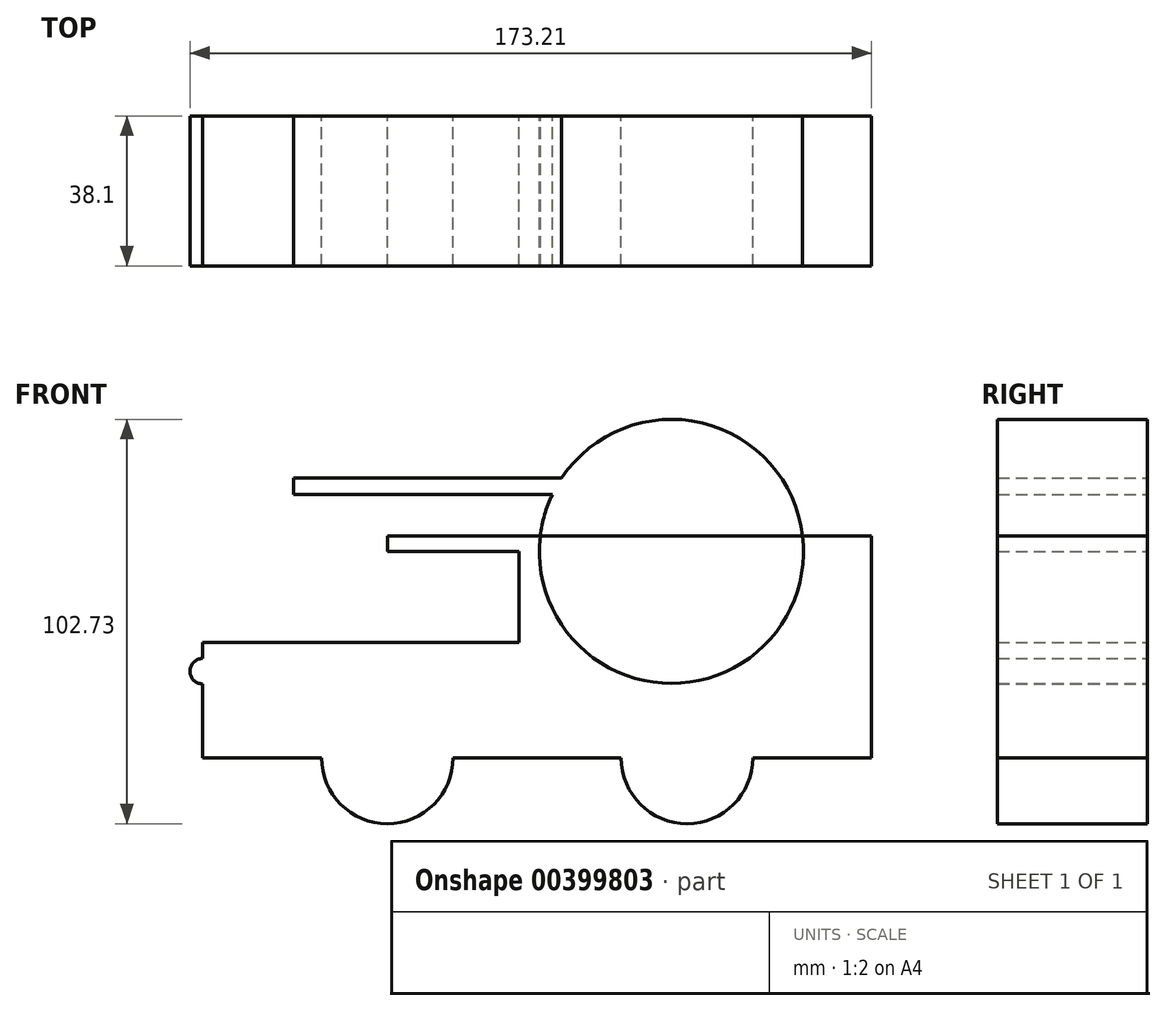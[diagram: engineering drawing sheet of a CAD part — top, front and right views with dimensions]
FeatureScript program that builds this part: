
annotation { "Feature Type Name" : "Feature", "Feature Type Description" : "" }
export const myFeature = defineFeature(function(context is Context, id is Id, definition is map)
    precondition{}
    {
        {
            var Q0;
            Q0=qCreatedBy(makeId("Front.planeOp"),FACE);
            var sketch = newSketch(context, id + "F0", { "sketchPlane" : qUnion([Q0])});
            skLineSegment(sketch, "E0.bottom", {"start": v(0, 0) * mm, "end": v(-46.94, 0) * mm});
            skLineSegment(sketch, "E0.top", {"start": v(0, 29.34) * mm, "end": v(-46.94, 29.34) * mm});
            skLineSegment(sketch, "E0.left", {"start": v(0, 0) * mm, "end": v(0, 29.34) * mm});
            skLineSegment(sketch, "E0.right", {"start": v(-46.94, 0) * mm, "end": v(-46.94, 29.34) * mm});
            skLineSegment(sketch, "E1.bottom", {"start": v(0, 0) * mm, "end": v(123.05, 0) * mm});
            skLineSegment(sketch, "E1.top", {"start": v(0, 52.46) * mm, "end": v(123.05, 52.46) * mm});
            skLineSegment(sketch, "E1.left", {"start": v(0, 0) * mm, "end": v(0, 52.46) * mm});
            skLineSegment(sketch, "E1.right", {"start": v(123.05, 0) * mm, "end": v(123.05, 52.46) * mm});
            skLineSegment(sketch, "E2.bottom", {"start": v(33.43, 52.46) * mm, "end": v(0, 52.46) * mm});
            skLineSegment(sketch, "E2.top", {"start": v(33.43, 29.34) * mm, "end": v(0, 29.34) * mm});
            skLineSegment(sketch, "E2.left", {"start": v(33.43, 52.46) * mm, "end": v(33.43, 29.34) * mm});
            skLineSegment(sketch, "E2.right", {"start": v(0, 52.46) * mm, "end": v(0, 29.34) * mm});
            skCircle(sketch, "E3", {"center": v(72.2, 52.46) * mm, "radius": 33.55 * mm});
            skLineSegment(sketch, "E4.bottom", {"start": v(50.5, 66.94) * mm, "end": v(-23.8, 66.94) * mm});
            skLineSegment(sketch, "E4.top", {"start": v(50.5, 71.09) * mm, "end": v(-23.8, 71.09) * mm});
            skLineSegment(sketch, "E4.left", {"start": v(50.5, 66.94) * mm, "end": v(50.5, 71.09) * mm});
            skLineSegment(sketch, "E4.right", {"start": v(-23.8, 66.94) * mm, "end": v(-23.8, 71.09) * mm});
            skCircle(sketch, "E5", {"center": v(0, 0) * mm, "radius": 16.72 * mm});
            skCircle(sketch, "E6", {"center": v(76.15, 0) * mm, "radius": 16.72 * mm});
            skLineSegment(sketch, "E7.bottom", {"start": v(0, 29.34) * mm, "end": v(-4.94, 29.34) * mm});
            skLineSegment(sketch, "E7.top", {"start": v(0, 56.38) * mm, "end": v(-4.94, 56.38) * mm});
            skLineSegment(sketch, "E7.left", {"start": v(0, 29.34) * mm, "end": v(0, 56.38) * mm});
            skLineSegment(sketch, "E7.right", {"start": v(-4.94, 29.34) * mm, "end": v(-4.94, 56.38) * mm});
            skLineSegment(sketch, "E8.bottom", {"start": v(0, 56.38) * mm, "end": v(33.43, 56.38) * mm});
            skLineSegment(sketch, "E8.top", {"start": v(0, 52.46) * mm, "end": v(33.43, 52.46) * mm});
            skLineSegment(sketch, "E8.left", {"start": v(0, 56.38) * mm, "end": v(0, 52.46) * mm});
            skLineSegment(sketch, "E8.right", {"start": v(33.43, 56.38) * mm, "end": v(33.43, 52.46) * mm});
            skLineSegment(sketch, "E9.bottom", {"start": v(33.43, 56.38) * mm, "end": v(123.05, 56.38) * mm});
            skLineSegment(sketch, "E9.top", {"start": v(33.43, 52.46) * mm, "end": v(123.05, 52.46) * mm});
            skLineSegment(sketch, "E9.right", {"start": v(123.05, 56.38) * mm, "end": v(123.05, 52.46) * mm});
            skCircle(sketch, "E10", {"center": v(-46.94, 22) * mm, "radius": 3.21 * mm});
            skSolve(sketch);
        }
        {
            var Q0;
            Q0=makeQuery(id+"F0.imprint","IMPRINT",FACE,{"disambiguationData":[TD([[makeQuery(id+"F0.imprint","IMPRINT",EDGE,{"derivedFrom":sQuery(id+"F0.wireOp",EDGE,"E0.top")}),1.0]])]});
            var Q1;
            {var subQ10=sQuery(id+"F0.wireOp",EDGE,"E1.right");Q1=makeQuery(id+"F0.imprint","IMPRINT",FACE,{"disambiguationData":[TD([[makeQuery(id+"F0.imprint","IMPRINT",EDGE,{"derivedFrom":subQ10}),1.0]])]});}
            var Q2;
            {var subQ0=sQuery(id+"F0.wireOp",EDGE,"E4.left");Q2=makeQuery(id+"F0.imprint","IMPRINT",FACE,{"disambiguationData":[TD([[makeQuery(id+"F0.imprint","IMPRINT",EDGE,{"derivedFrom":subQ0}),-1.0]])]});}
            var Q3;
            {var subQ0=sQuery(id+"F0.wireOp",EDGE,"E9.bottom");var subQ1=sQuery(id+"F0.wireOp",EDGE,"E3");var subQ2=makeQuery(id+"F0.imprint","INTERSECT",VERTEX,{"disambiguationData":[OD(0.0)],"derivedFrom":[subQ1,subQ0]});Q3=makeQuery(id+"F0.imprint","IMPRINT",FACE,{"disambiguationData":[TD([[makeQuery(id+"F0.imprint","IMPRINT",EDGE,{"disambiguationData":[TD([[subQ2,1.0]])],"derivedFrom":subQ1}),1.0]])]});}
            var Q4;
            {var subQ0=sQuery(id+"F0.wireOp",EDGE,"E9.top");var subQ1=sQuery(id+"F0.wireOp",EDGE,"E3");var subQ2=makeQuery(id+"F0.imprint","INTERSECT",VERTEX,{"disambiguationData":[OD(0.0)],"derivedFrom":[subQ1,subQ0]});Q4=makeQuery(id+"F0.imprint","IMPRINT",FACE,{"disambiguationData":[TD([[makeQuery(id+"F0.imprint","IMPRINT",EDGE,{"disambiguationData":[TD([[subQ2,1.0]])],"derivedFrom":subQ1}),1.0]])]});}
            var Q5;
            {var subQ5=sQuery(id+"F0.wireOp",EDGE,"E9.right");Q5=makeQuery(id+"F0.imprint","IMPRINT",FACE,{"disambiguationData":[TD([[makeQuery(id+"F0.imprint","IMPRINT",EDGE,{"derivedFrom":subQ5}),-1.0]])]});}
            var Q6;
            {var subQ5=sQuery(id+"F0.wireOp",EDGE,"E8.right");Q6=makeQuery(id+"F0.imprint","IMPRINT",FACE,{"disambiguationData":[TD([[makeQuery(id+"F0.imprint","IMPRINT",EDGE,{"derivedFrom":subQ5}),1.0]])]});}
            var Q7;
            {var subQ5=sQuery(id+"F0.wireOp",EDGE,"E4.left");Q7=makeQuery(id+"F0.imprint","IMPRINT",FACE,{"disambiguationData":[TD([[makeQuery(id+"F0.imprint","IMPRINT",EDGE,{"derivedFrom":subQ5}),1.0]])]});}
            var Q8;
            Q8=makeQuery(id+"F0.imprint","IMPRINT",FACE,{"disambiguationData":[TD([[makeQuery(id+"F0.imprint","IMPRINT",EDGE,{"derivedFrom":sQuery(id+"F0.wireOp",EDGE,"E8.bottom")}),-1.0]])]});
            var Q9;
            Q9=makeQuery(id+"F0.imprint","IMPRINT",FACE,{"disambiguationData":[TD([[makeQuery(id+"F0.imprint","IMPRINT",EDGE,{"derivedFrom":sQuery(id+"F0.wireOp",EDGE,"E7.bottom")}),-1.0]])]});
            var Q10;
            {var subQ5=sQuery(id+"F0.wireOp",EDGE,"E4.right");Q10=makeQuery(id+"F0.imprint","IMPRINT",FACE,{"disambiguationData":[TD([[makeQuery(id+"F0.imprint","IMPRINT",EDGE,{"derivedFrom":subQ5}),-1.0]])]});}
            var Q11;
            {var subQ1=sQuery(id+"F0.wireOp",EDGE,"E0.bottom");var subQ3=sQuery(id+"F0.wireOp",EDGE,"E5");var subQ4=makeQuery(id+"F0.imprint","INTERSECT",VERTEX,{"derivedFrom":[subQ1,subQ3]});Q11=makeQuery(id+"F0.imprint","IMPRINT",FACE,{"disambiguationData":[TD([[makeQuery(id+"F0.imprint","IMPRINT",EDGE,{"disambiguationData":[TD([[subQ4,1.0]])],"derivedFrom":subQ3}),1.0]])]});}
            var Q12;
            {var subQ1=sQuery(id+"F0.wireOp",EDGE,"E1.bottom");var subQ3=sQuery(id+"F0.wireOp",EDGE,"E5");var subQ4=makeQuery(id+"F0.imprint","INTERSECT",VERTEX,{"derivedFrom":[subQ1,subQ3]});Q12=makeQuery(id+"F0.imprint","IMPRINT",FACE,{"disambiguationData":[TD([[makeQuery(id+"F0.imprint","IMPRINT",EDGE,{"disambiguationData":[TD([[subQ4,-1.0]])],"derivedFrom":subQ3}),1.0]])]});}
            var Q13;
            {var subQ1=sQuery(id+"F0.wireOp",EDGE,"E0.bottom");var subQ3=sQuery(id+"F0.wireOp",EDGE,"E5");var subQ4=makeQuery(id+"F0.imprint","INTERSECT",VERTEX,{"derivedFrom":[subQ1,subQ3]});Q13=makeQuery(id+"F0.imprint","IMPRINT",FACE,{"disambiguationData":[TD([[makeQuery(id+"F0.imprint","IMPRINT",EDGE,{"disambiguationData":[TD([[subQ4,-1.0]])],"derivedFrom":subQ3}),1.0]])]});}
            var Q14;
            {var subQ0=sQuery(id+"F0.wireOp",EDGE,"E6");var subQ1=sQuery(id+"F0.wireOp",EDGE,"E1.bottom");var subQ2=makeQuery(id+"F0.imprint","INTERSECT",VERTEX,{"disambiguationData":[OD(0.0)],"derivedFrom":[subQ1,subQ0]});Q14=makeQuery(id+"F0.imprint","IMPRINT",FACE,{"disambiguationData":[TD([[makeQuery(id+"F0.imprint","IMPRINT",EDGE,{"disambiguationData":[TD([[subQ2,-1.0]])],"derivedFrom":subQ1}),1.0]])]});}
            var Q15;
            {var subQ0=sQuery(id+"F0.wireOp",EDGE,"E6");var subQ1=sQuery(id+"F0.wireOp",EDGE,"E1.bottom");var subQ2=makeQuery(id+"F0.imprint","INTERSECT",VERTEX,{"disambiguationData":[OD(0.0)],"derivedFrom":[subQ1,subQ0]});Q15=makeQuery(id+"F0.imprint","IMPRINT",FACE,{"disambiguationData":[TD([[makeQuery(id+"F0.imprint","IMPRINT",EDGE,{"disambiguationData":[TD([[subQ2,-1.0]])],"derivedFrom":subQ1}),-1.0]])]});}
            var Q16;
            {var subQ0=sQuery(id+"F0.wireOp",EDGE,"E10");var subQ1=sQuery(id+"F0.wireOp",EDGE,"E0.right");var subQ2=makeQuery(id+"F0.imprint","INTERSECT",VERTEX,{"disambiguationData":[OD(0.0)],"derivedFrom":[subQ1,subQ0]});Q16=makeQuery(id+"F0.imprint","IMPRINT",FACE,{"disambiguationData":[TD([[makeQuery(id+"F0.imprint","IMPRINT",EDGE,{"disambiguationData":[TD([[subQ2,-1.0]])],"derivedFrom":subQ1}),1.0]])]});}
            var Q17;
            {var subQ0=sQuery(id+"F0.wireOp",EDGE,"E10");var subQ1=sQuery(id+"F0.wireOp",EDGE,"E0.right");var subQ2=makeQuery(id+"F0.imprint","INTERSECT",VERTEX,{"disambiguationData":[OD(0.0)],"derivedFrom":[subQ1,subQ0]});Q17=makeQuery(id+"F0.imprint","IMPRINT",FACE,{"disambiguationData":[TD([[makeQuery(id+"F0.imprint","IMPRINT",EDGE,{"disambiguationData":[TD([[subQ2,-1.0]])],"derivedFrom":subQ1}),-1.0]])]});}
            extrude(context, id + "F1", {"entities" : qUnion([Q0, Q1, Q2, Q3, Q4, Q5, Q6, Q7, Q8, Q9, Q10, Q11, Q12, Q13, Q14, Q15, Q16, Q17]), "depth" : 38.1 * mm});
        }
    });
